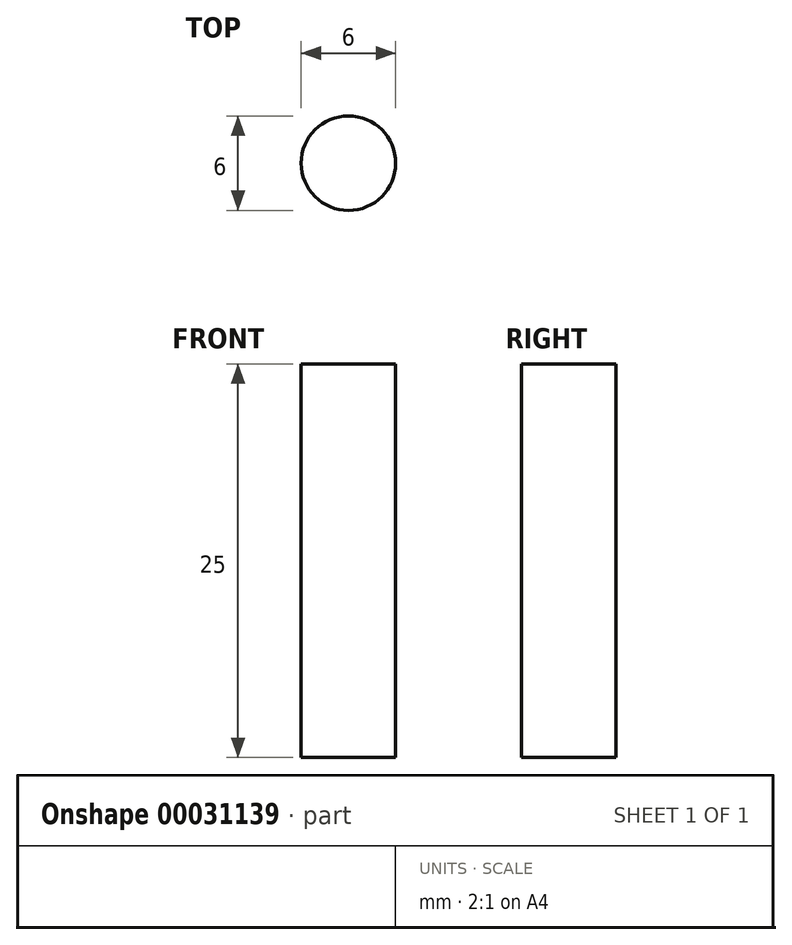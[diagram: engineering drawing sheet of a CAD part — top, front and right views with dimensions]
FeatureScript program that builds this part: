
annotation { "Feature Type Name" : "Feature", "Feature Type Description" : "" }
export const myFeature = defineFeature(function(context is Context, id is Id, definition is map)
    precondition{}
    {
        {
            var Q0;
            Q0=qCreatedBy(makeId("Top.planeOp"),FACE);
            var sketch = newSketch(context, id + "F0", { "sketchPlane" : qUnion([Q0])});
            skCircle(sketch, "E0", {"center": v(0, 0) * mm, "radius": 3 * mm});
            skSolve(sketch);
        }
        {
            var Q0;
            Q0 = qSketchRegion(id + "F0", true);
            var Q1;
            Q1=makeQuery(id+"F0.imprint","IMPRINT",FACE,{"disambiguationData":[TD([[makeQuery(id+"F0.imprint","IMPRINT",EDGE,{"derivedFrom":sQuery(id+"F0.wireOp",EDGE,"E0")}),1.0]])]});
            extrude(context, id + "F1", {"entities" : qUnion([Q0, Q1]), "depth" : 25 * mm});
        }
    });
